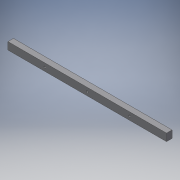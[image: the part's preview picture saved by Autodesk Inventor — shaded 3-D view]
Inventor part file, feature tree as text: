
AUTODESK INVENTOR PART (.ipt)
format: ipt  version: 2019 (Build 230136000, 136)  size: 162,816 bytes
history: native  units: in
note: dims shown in document units (in); Inventor stores cm internally (conversion verified against a paired STEP export)
features: extrude x6, sketch x6, other x2, reference x1, projected_geometry x1, helix x1
ambient origin geometry x8: Origin, YZ Plane, XZ Plane, XY Plane, X Axis, Y Axis, Z Axis, Center Point
bodies: Solid1 (feature_tree)
feature tree (17):
  extrude  "Extrusion1"  Depth=0.5906in TaperAngle=0.0deg
  extrude  "Extrusion2"  Depth=3.937in
  extrude  "Extrusion3"  Depth=3.937in
  extrude  "Extrusion4"  Depth=0.3937in TaperAngle=0.0deg
  extrude  "Extrusion5"  Depth=16.9291in
  extrude  "Extrusion6"  Depth=0.5906in
  sketch  "Sketch1"  dims[d1=0.7874in d2=0.5906in d3=0.0in]
  reference  "Reference1"
  sketch  "Sketch2"  dims[d4=0.1969in d5=3.937in]
  sketch  "Sketch3"  dims[d6=0.1969in d7=3.937in]
  sketch  "Sketch4"  dims[d8=0.1969in d9=0.3937in d10=0.0in]
  sketch  "Sketch5"  dims[d11=16.9291in d12=0.4331in]
  projected_geometry  "Projected Loop1"
  sketch  "Sketch6"  dims[d13=0.4331in d14=0.4331in d15=0.2362in d16=0.0in d17=0.1654in d18=0.1575in d19=0.5906in d20=0.0in d21=0.5906in d22=0.0in d23=0.1378in d24=1.5748in d26=3.937in d27=0.3937in d29=1.0in d31=2.5591in d32=0.5906in d33=0.0in]
  other  "<userpath>\Documents\CAD Files\Helix DLP\Helix DLP.iam"
  helix  "Helix DLP.iam"  [1 undecoded]
  other  "Tank2:1"
note: 1 required parameter value undecoded (feature->parameter linkage not recoverable at this tier; creation-order binding heuristic only, values carry confidence <= 0.55)
